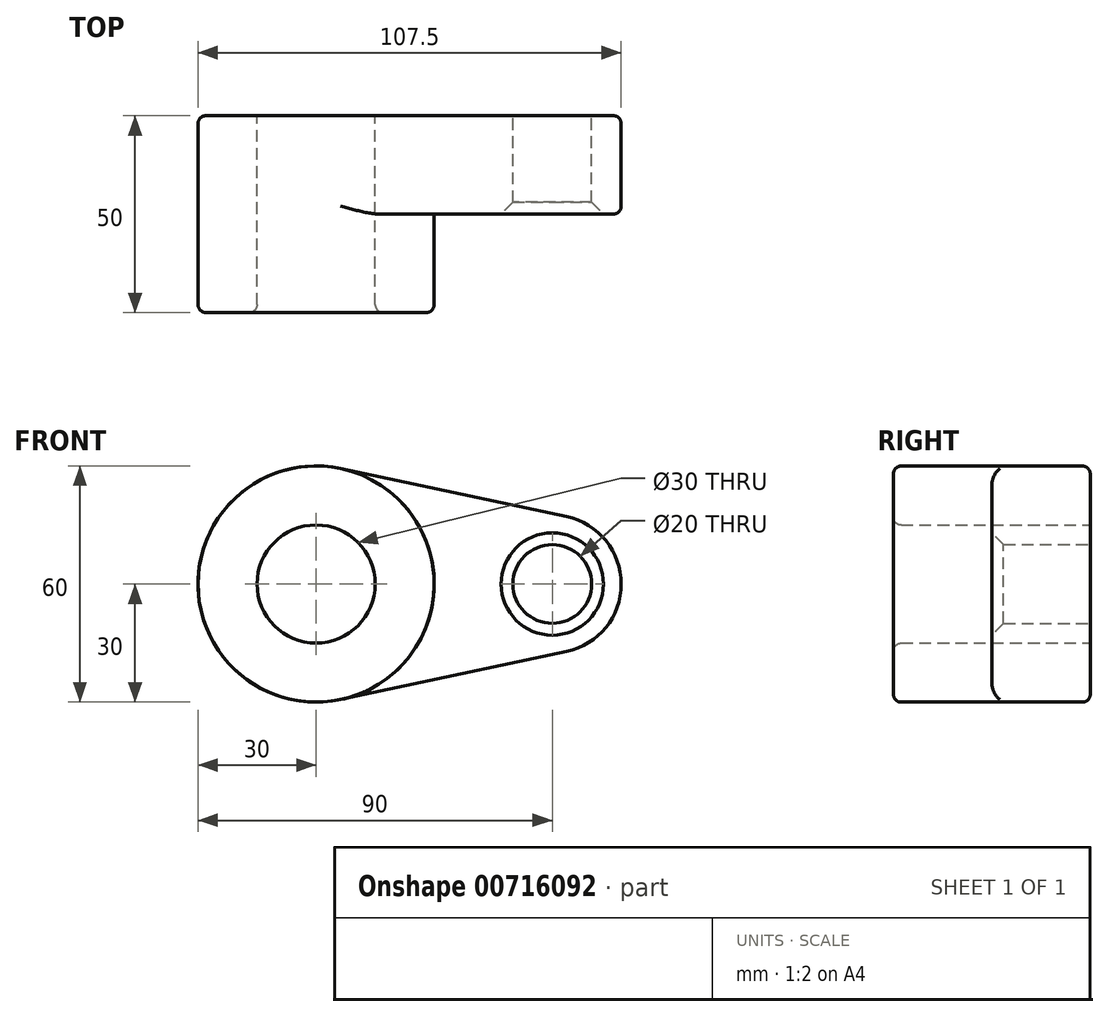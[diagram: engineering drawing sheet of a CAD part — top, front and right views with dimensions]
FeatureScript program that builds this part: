
annotation { "Feature Type Name" : "Feature", "Feature Type Description" : "" }
export const myFeature = defineFeature(function(context is Context, id is Id, definition is map)
    precondition{}
    {
        {
            var Q0;
            Q0=qCreatedBy(makeId("Front.planeOp"),FACE);
            var sketch = newSketch(context, id + "F0", { "sketchPlane" : qUnion([Q0])});
            skCircle(sketch, "E0", {"center": v(0, 0) * mm, "radius": 30 * mm});
            skCircle(sketch, "E1", {"center": v(60, 0) * mm, "radius": 17.5 * mm});
            skLineSegment(sketch, "E2", {"start": v(6.25, 29.34) * mm, "end": v(63.65, 17.12) * mm});
            skLineSegment(sketch, "E3", {"start": v(6.25, -29.34) * mm, "end": v(63.65, -17.12) * mm});
            skCircle(sketch, "E4", {"center": v(0, 0) * mm, "radius": 15 * mm});
            skCircle(sketch, "E5", {"center": v(60, 0) * mm, "radius": 10 * mm});
            skSolve(sketch);
        }
        {
            var Q0;
            Q0 = qSketchRegion(id + "F0", true);
            extrude(context, id + "F1", {"entities" : qUnion([Q0]), "depth" : 25 * mm, "offsetDistance" : 25 * mm});
        }
        {
            var Q0;
            Q0=makeQuery(id+"F0.imprint","IMPRINT",FACE,{"disambiguationData":[TD([[makeQuery(id+"F0.imprint","IMPRINT",EDGE,{"derivedFrom":sQuery(id+"F0.wireOp",EDGE,"E4")}),-1.0]])]});
            extrude(context, id + "F2", {"entities" : qUnion([Q0]), "operationType" : NewBodyOperationType.ADD, "depth" : 50 * mm, "offsetDistance" : 25 * mm});
        }
        {
            var Q0;
            Q0=makeQuery(id+"F1.opExtrude","SWEPT_FACE",FACE,{"disambiguationData":[OSD([sQuery(id+"F0.wireOp",EDGE,"E3")])]});
            var Q1;
            Q1=makeQuery(id+"F2.opExtrude","CAP_FACE",FACE,{"disambiguationData":[OSD([sQuery(id+"F0.wireOp",EDGE,"E0"),sQuery(id+"F0.wireOp",EDGE,"E4")])],"isStart":false});
            fillet(context, id + "F3", {"entities" : qUnion([Q0, Q1]), "radius" : 2 * mm, "tangentPropagation" : true, "allowEdgeOverflow" : false});
        }
        {
            var Q0;
            {var subQ0=sQuery(id+"F0.wireOp",EDGE,"E4");Q0=makeQuery(id+"F3.opFillet","BLEND_EDGE",EDGE,{"blendedFrom":[makeQuery(id+"F2.opExtrude","CAP_EDGE",EDGE,{"disambiguationData":[OSD([subQ0])],"isStart":false}),makeQuery(id+"F2.boolean.opBoolean","MERGE",FACE,{"derivedFrom":[makeQuery(id+"F1.opExtrude","SWEPT_FACE",FACE,{"disambiguationData":[OSD([subQ0])]}),makeQuery(id+"F2.opExtrude","SWEPT_FACE",FACE,{"disambiguationData":[OSD([subQ0])]})]})],"blendedInto":[makeQuery(id+"F2.boolean.opBoolean","MERGE",FACE,{"derivedFrom":[makeQuery(id+"F1.opExtrude","SWEPT_FACE",FACE,{"disambiguationData":[OSD([subQ0])]}),makeQuery(id+"F2.opExtrude","SWEPT_FACE",FACE,{"disambiguationData":[OSD([subQ0])]})]})]});}
            var Q1;
            Q1=makeQuery(id+"F1.opExtrude","CAP_EDGE",EDGE,{"disambiguationData":[OSD([sQuery(id+"F0.wireOp",EDGE,"E5")])],"isStart":false});
            chamfer(context, id + "F4", {"entities" : qUnion([Q0, Q1]), "width" : 3 * mm, "tangentPropagation" : true});
        }
    });
